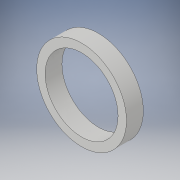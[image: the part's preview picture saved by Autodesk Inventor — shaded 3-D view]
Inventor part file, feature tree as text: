
AUTODESK INVENTOR PART (.ipt)
format: ipt  version: 2019 (Build 230136000, 136)  size: 103,936 bytes
history: native  units: mm
features: extrude x2, sketch x2
ambient origin geometry x8: Origin, YZ Plane, XZ Plane, XY Plane, X Axis, Y Axis, Z Axis, Center Point
bodies: Solid1 (feature_tree)
feature tree (4):
  extrude  "Extrusion1"  Depth=6.0mm TaperAngle=0.0deg
  extrude  "Extrusion2"  Depth=6.0mm TaperAngle=0.0deg
  sketch  "Sketch1"  dims[d0=32.0mm d1=6.0mm d2=0.0mm]
  sketch  "Sketch2"  dims[d3=26.0mm d4=6.0mm d5=0.0mm]
